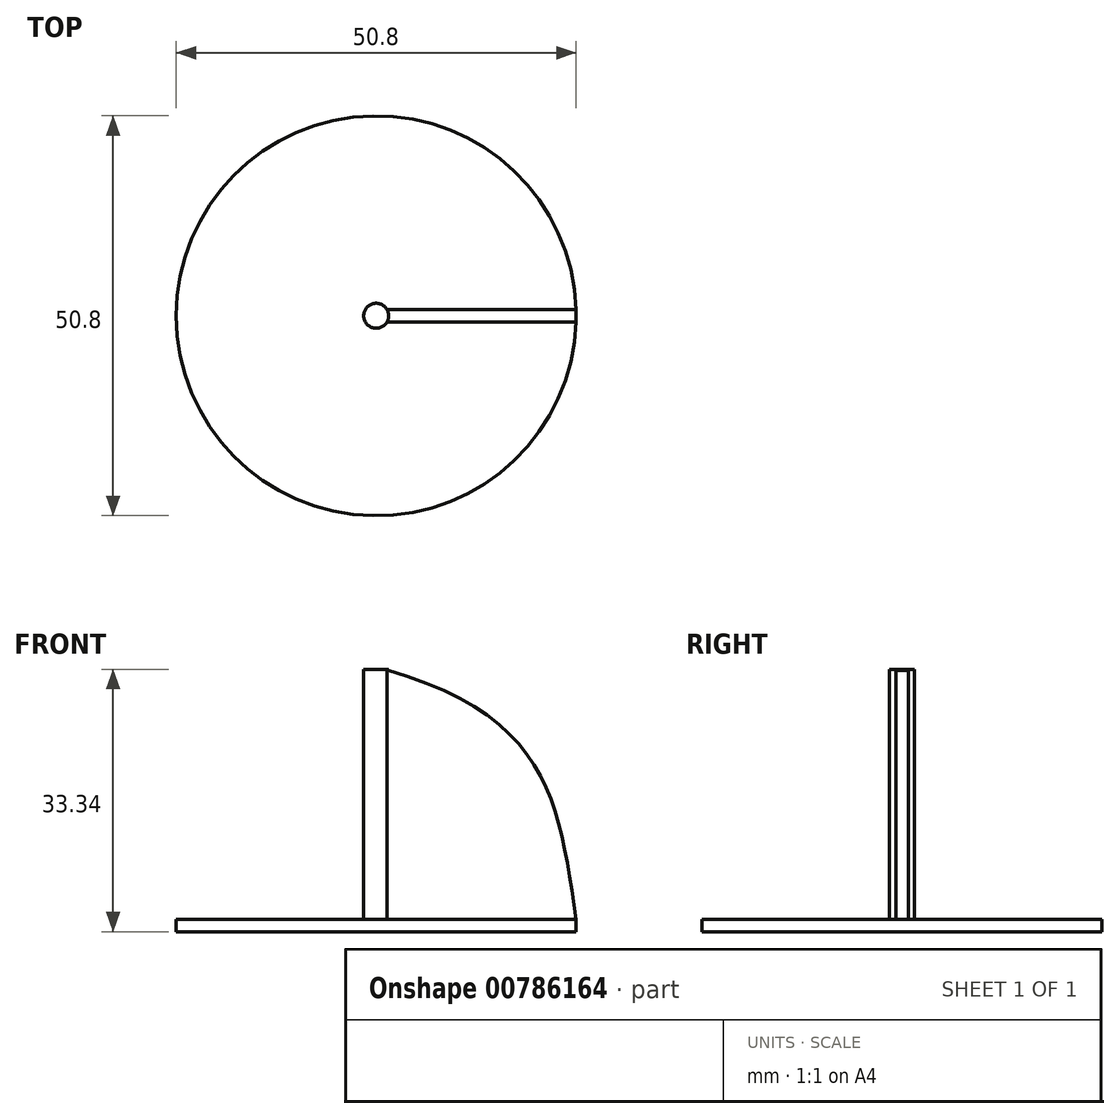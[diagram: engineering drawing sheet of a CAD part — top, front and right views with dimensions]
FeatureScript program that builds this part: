
annotation { "Feature Type Name" : "Feature", "Feature Type Description" : "" }
export const myFeature = defineFeature(function(context is Context, id is Id, definition is map)
    precondition{}
    {
        {
            var Q0;
            Q0=qCreatedBy(makeId("Top.planeOp"),FACE);
            var sketch = newSketch(context, id + "F0", { "sketchPlane" : qUnion([Q0])});
            skCircle(sketch, "E0", {"center": v(0, 0) * mm, "radius": 25.4 * mm});
            skSolve(sketch);
        }
        {
            var Q0;
            Q0 = qSketchRegion(id + "F0", true);
            extrude(context, id + "F1", {"entities" : qUnion([Q0]), "depth" : 1.59 * mm, "offsetDistance" : 25.4 * mm});
        }
        {
            var Q0;
            Q0=makeQuery(id+"F1.opExtrude","CAP_FACE",FACE,{"disambiguationData":[OSD([sQuery(id+"F0.wireOp",EDGE,"E0")])],"isStart":false});
            var sketch = newSketch(context, id + "F2", { "sketchPlane" : qUnion([Q0])});
            skCircle(sketch, "E1", {"center": v(0, 0) * mm, "radius": 1.59 * mm});
            skSolve(sketch);
        }
        {
            var Q0;
            Q0 = qSketchRegion(id + "F2", true);
            extrude(context, id + "F3", {"entities" : qUnion([Q0]), "operationType" : NewBodyOperationType.ADD, "depth" : 31.75 * mm, "offsetDistance" : 25.4 * mm});
        }
        {
            var Q0;
            Q0=qCreatedBy(makeId("Front.planeOp"),FACE);
            var sketch = newSketch(context, id + "F4", { "sketchPlane" : qUnion([Q0])});
            skLineSegment(sketch, "E2.0", {"start": v(-25.4, 1.59) * mm, "end": v(25.4, 1.59) * mm, "construction": true});
            skLineSegment(sketch, "E3", {"start": v(1.02, 1.59) * mm, "end": v(1.02, 33.34) * mm});
            skLineSegment(sketch, "E4.0", {"start": v(-1.59, 33.34) * mm, "end": v(1.59, 33.34) * mm, "construction": true});
            skPoint(sketch, "E5", {"position": v(0, 33.34) * mm});
            skLineSegment(sketch, "E6", {"start": v(1.02, 1.59) * mm, "end": v(25.4, 1.59) * mm});
            skFitSpline(sketch, "E7", {"points": [v(1.02, 33.34) * mm, v(25.4, 1.59) * mm], "startDerivative": vector(64.17, -17.72) * mm, "endDerivative": vector(6.56, -42.88) * mm});
            skSolve(sketch);
        }
        {
            var Q0;
            Q0 = qSketchRegion(id + "F4", true);
            extrude(context, id + "F5", {"entities" : qUnion([Q0]), "operationType" : NewBodyOperationType.ADD, "endBound" : BoundingType.SYMMETRIC, "depth" : 1.59 * mm, "offsetDistance" : 25.4 * mm});
        }
    });
